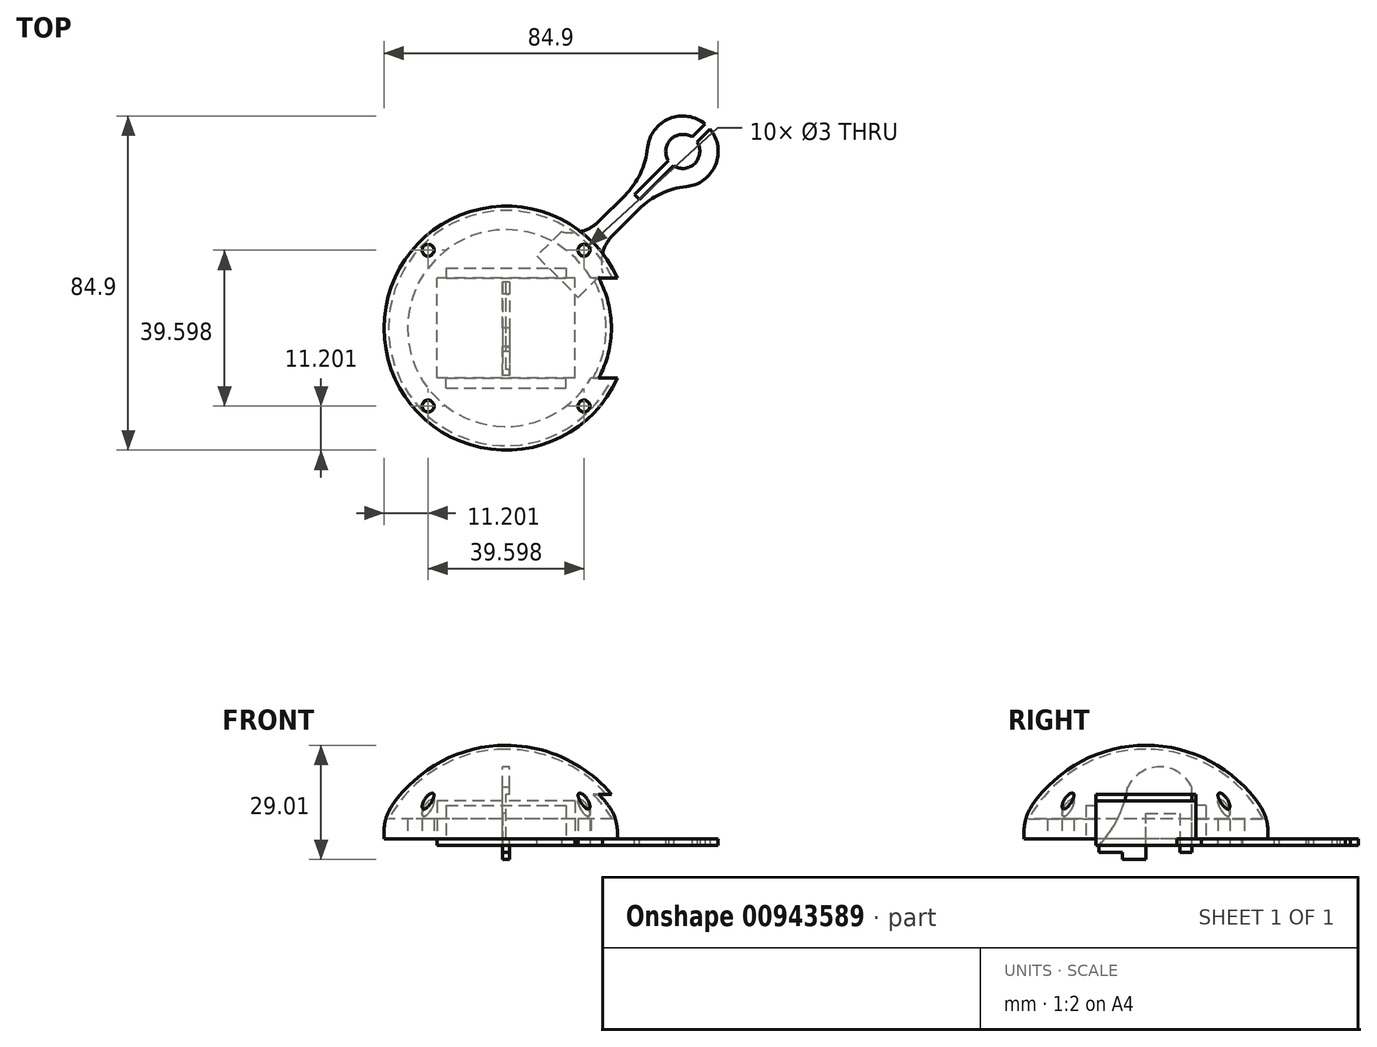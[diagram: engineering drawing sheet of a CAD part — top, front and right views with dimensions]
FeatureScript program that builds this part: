
annotation { "Feature Type Name" : "Feature", "Feature Type Description" : "" }
export const myFeature = defineFeature(function(context is Context, id is Id, definition is map)
    precondition{}
    {
        {
            var Q0;
            Q0=qCreatedBy(makeId("Top.planeOp"),FACE);
            var sketch = newSketch(context, id + "F0", { "sketchPlane" : qUnion([Q0])});
            skCircle(sketch, "E0", {"center": v(0, 0) * mm, "radius": 25 * mm, "construction": true});
            skArc(sketch, "E1", {"start": v(-25.2, 12.18) * mm, "mid": v(-26.92, 7.7) * mm, "end": v(-27.84, 3) * mm});
            skLineSegment(sketch, "E2", {"start": v(-44.9, -44.9) * mm, "end": v(44.9, 44.9) * mm, "construction": true});
            skLineSegment(sketch, "E3", {"start": v(-44.9, 44.9) * mm, "end": v(44.9, -44.9) * mm, "construction": true});
            skCircle(sketch, "E4", {"center": v(0, 28) * mm, "radius": 1.5 * mm});
            skCircle(sketch, "E5", {"center": v(-19.8, 19.8) * mm, "radius": 1.5 * mm});
            skCircle(sketch, "E6", {"center": v(-28, 0) * mm, "radius": 1.5 * mm});
            skCircle(sketch, "E7", {"center": v(-19.8, -19.8) * mm, "radius": 1.5 * mm});
            skCircle(sketch, "E8", {"center": v(0, -28) * mm, "radius": 1.5 * mm});
            skCircle(sketch, "E9", {"center": v(19.8, -19.8) * mm, "radius": 1.5 * mm});
            skCircle(sketch, "E10", {"center": v(28, 0) * mm, "radius": 1.5 * mm});
            skCircle(sketch, "E11", {"center": v(19.8, 19.8) * mm, "radius": 1.5 * mm});
            skArc(sketch, "E12", {"start": v(3, 27.84) * mm, "mid": v(0, 31) * mm, "end": v(-3, 27.84) * mm});
            skArc(sketch, "E13", {"start": v(27.84, -3) * mm, "mid": v(31, 0) * mm, "end": v(27.84, 3) * mm});
            skArc(sketch, "E14", {"start": v(-3, -27.84) * mm, "mid": v(0, -31) * mm, "end": v(3, -27.84) * mm});
            skArc(sketch, "E15", {"start": v(-27.84, 3) * mm, "mid": v(-31, 0) * mm, "end": v(-27.84, -3) * mm});
            skArc(sketch, "E16.trimOffspring", {"start": v(12.18, 25.2) * mm, "mid": v(7.7, 26.92) * mm, "end": v(3, 27.84) * mm});
            skArc(sketch, "E17.trimOffspring", {"start": v(3, -27.84) * mm, "mid": v(7.7, -26.92) * mm, "end": v(12.18, -25.2) * mm});
            skArc(sketch, "E18.trimOffspring", {"start": v(-12.18, -25.2) * mm, "mid": v(-7.7, -26.92) * mm, "end": v(-3, -27.84) * mm});
            skArc(sketch, "E19", {"start": v(45.82, 35.95) * mm, "mid": v(51.27, 51.27) * mm, "end": v(35.95, 45.82) * mm});
            skArc(sketch, "E20", {"start": v(35.95, -45.82) * mm, "mid": v(51.27, -51.27) * mm, "end": v(45.82, -35.95) * mm});
            skArc(sketch, "E21", {"start": v(-45.82, -35.95) * mm, "mid": v(-51.27, -51.27) * mm, "end": v(-35.95, -45.82) * mm});
            skArc(sketch, "E22", {"start": v(-35.95, 45.82) * mm, "mid": v(-51.27, 51.27) * mm, "end": v(-45.82, 35.95) * mm});
            skLineSegment(sketch, "E23", {"start": v(23.6, 27.14) * mm, "end": v(30.2, 33.73) * mm});
            skLineSegment(sketch, "E24", {"start": v(33.73, 30.2) * mm, "end": v(27.14, 23.6) * mm});
            skLineSegment(sketch, "E25", {"start": v(33.73, -30.2) * mm, "end": v(27.14, -23.6) * mm});
            skLineSegment(sketch, "E26", {"start": v(30.2, -33.73) * mm, "end": v(23.6, -27.14) * mm});
            skLineSegment(sketch, "E27", {"start": v(-30.2, -33.73) * mm, "end": v(-23.6, -27.14) * mm});
            skLineSegment(sketch, "E28", {"start": v(-33.73, -30.2) * mm, "end": v(-27.14, -23.6) * mm});
            skLineSegment(sketch, "E29", {"start": v(-33.73, 30.2) * mm, "end": v(-27.14, 23.6) * mm});
            skLineSegment(sketch, "E30", {"start": v(-30.2, 33.73) * mm, "end": v(-23.6, 27.14) * mm});
            skCircle(sketch, "E31", {"center": v(44.9, 44.9) * mm, "radius": 4.33 * mm});
            skCircle(sketch, "E32", {"center": v(44.9, -44.9) * mm, "radius": 4.33 * mm});
            skCircle(sketch, "E33", {"center": v(-44.9, -44.9) * mm, "radius": 4.33 * mm});
            skCircle(sketch, "E34", {"center": v(-44.9, 44.9) * mm, "radius": 4.33 * mm});
            skPoint(sketch, "E35.visualSharp", {"position": v(40.56, -37.02) * mm});
            skArc(sketch, "E35.filletArc", {"start": v(33.73, -30.2) * mm, "mid": v(39.28, -34.11) * mm, "end": v(45.82, -35.95) * mm});
            skPoint(sketch, "E36.visualSharp", {"position": v(37.02, -40.56) * mm});
            skArc(sketch, "E36.filletArc", {"start": v(35.95, -45.82) * mm, "mid": v(34.11, -39.28) * mm, "end": v(30.2, -33.73) * mm});
            skPoint(sketch, "E37.visualSharp", {"position": v(-37.02, -40.56) * mm});
            skArc(sketch, "E37.filletArc", {"start": v(-30.2, -33.73) * mm, "mid": v(-34.11, -39.28) * mm, "end": v(-35.95, -45.82) * mm});
            skPoint(sketch, "E38.visualSharp", {"position": v(-40.56, -37.02) * mm});
            skArc(sketch, "E38.filletArc", {"start": v(-45.82, -35.95) * mm, "mid": v(-39.28, -34.11) * mm, "end": v(-33.73, -30.2) * mm});
            skPoint(sketch, "E39.visualSharp", {"position": v(-40.56, 37.02) * mm});
            skArc(sketch, "E39.filletArc", {"start": v(-33.73, 30.2) * mm, "mid": v(-39.28, 34.11) * mm, "end": v(-45.82, 35.95) * mm});
            skPoint(sketch, "E40.visualSharp", {"position": v(-37.02, 40.56) * mm});
            skArc(sketch, "E40.filletArc", {"start": v(-35.95, 45.82) * mm, "mid": v(-34.11, 39.28) * mm, "end": v(-30.2, 33.73) * mm});
            skPoint(sketch, "E41.visualSharp", {"position": v(37.02, 40.56) * mm});
            skArc(sketch, "E41.filletArc", {"start": v(30.2, 33.73) * mm, "mid": v(34.11, 39.28) * mm, "end": v(35.95, 45.82) * mm});
            skPoint(sketch, "E42.visualSharp", {"position": v(40.56, 37.02) * mm});
            skArc(sketch, "E42.filletArc", {"start": v(45.82, 35.95) * mm, "mid": v(39.28, 34.11) * mm, "end": v(33.73, 30.2) * mm});
            skArc(sketch, "E43.filletArc", {"start": v(23.6, -27.14) * mm, "mid": v(18.2, -24.35) * mm, "end": v(12.18, -25.2) * mm});
            skArc(sketch, "E44", {"start": v(-12.18, -25.2) * mm, "mid": v(0, -28) * mm, "end": v(12.18, -25.2) * mm});
            skArc(sketch, "E45.filletArc", {"start": v(-12.18, -25.2) * mm, "mid": v(-18.2, -24.35) * mm, "end": v(-23.6, -27.14) * mm});
            skArc(sketch, "E46.filletArc", {"start": v(-25.2, 12.18) * mm, "mid": v(-24.35, 18.2) * mm, "end": v(-27.14, 23.6) * mm});
            skArc(sketch, "E47.filletArc", {"start": v(12.18, 25.2) * mm, "mid": v(18.2, 24.35) * mm, "end": v(23.6, 27.14) * mm});
            skPoint(sketch, "E48.visualSharp", {"position": v(-21.49, -17.95) * mm});
            skArc(sketch, "E48.filletArc", {"start": v(-27.14, -23.6) * mm, "mid": v(-24.35, -18.2) * mm, "end": v(-25.2, -12.18) * mm});
            skArc(sketch, "E49.trimOffspring", {"start": v(25.2, -12.18) * mm, "mid": v(26.92, -7.7) * mm, "end": v(27.84, -3) * mm});
            skPoint(sketch, "E50.visualSharp", {"position": v(21.49, -17.95) * mm});
            skArc(sketch, "E50.filletArc", {"start": v(25.2, -12.18) * mm, "mid": v(24.35, -18.2) * mm, "end": v(27.14, -23.6) * mm});
            skArc(sketch, "E51.trimOffspring", {"start": v(27.84, 3) * mm, "mid": v(26.92, 7.7) * mm, "end": v(25.2, 12.18) * mm});
            skPoint(sketch, "E52.visualSharp", {"position": v(21.49, 17.95) * mm});
            skArc(sketch, "E52.filletArc", {"start": v(27.14, 23.6) * mm, "mid": v(24.35, 18.2) * mm, "end": v(25.2, 12.18) * mm});
            skArc(sketch, "E53.trimOffspring", {"start": v(-3, 27.84) * mm, "mid": v(-7.7, 26.92) * mm, "end": v(-12.18, 25.2) * mm});
            skPoint(sketch, "E54.visualSharp", {"position": v(-17.95, 21.49) * mm});
            skArc(sketch, "E54.filletArc", {"start": v(-23.6, 27.14) * mm, "mid": v(-18.2, 24.35) * mm, "end": v(-12.18, 25.2) * mm});
            skArc(sketch, "E55.trimOffspring", {"start": v(-27.84, -3) * mm, "mid": v(-26.92, -7.7) * mm, "end": v(-25.2, -12.18) * mm});
            skSolve(sketch);
        }
        {
            var Q0;
            Q0 = qSketchRegion(id + "F0", true);
            extrude(context, id + "F1", {"entities" : qUnion([Q0]), "depth" : 1.7 * mm, "offsetDistance" : 25 * mm});
        }
        {
            var Q0;
            Q0=qCreatedBy(makeId("Top.planeOp"),FACE);
            var sketch = newSketch(context, id + "F2", { "sketchPlane" : qUnion([Q0])});
            skLineSegment(sketch, "E56", {"start": v(0, 0) * mm, "end": v(-50.91, -50.91) * mm, "construction": true});
            skLineSegment(sketch, "E57", {"start": v(-44.03, -45.3) * mm, "end": v(-36.96, -38.23) * mm});
            skLineSegment(sketch, "E58", {"start": v(-36.96, -38.23) * mm, "end": v(-38.23, -36.96) * mm});
            skLineSegment(sketch, "E59", {"start": v(-38.23, -36.96) * mm, "end": v(-45.3, -44.03) * mm});
            skLineSegment(sketch, "E60", {"start": v(-45.3, -44.03) * mm, "end": v(-44.03, -45.3) * mm});
            skLineSegment(sketch, "E61.MirrorCS", {"start": v(-36.96, 38.23) * mm, "end": v(-38.23, 36.96) * mm});
            skLineSegment(sketch, "E62.MirrorCS", {"start": v(-45.3, 44.03) * mm, "end": v(-44.03, 45.3) * mm});
            skLineSegment(sketch, "E63.MirrorCS", {"start": v(-44.03, 45.3) * mm, "end": v(-36.96, 38.23) * mm});
            skLineSegment(sketch, "E64.MirrorCS", {"start": v(-38.23, 36.96) * mm, "end": v(-45.3, 44.03) * mm});
            skLineSegment(sketch, "E65.MirrorCS", {"start": v(45.3, -44.03) * mm, "end": v(44.03, -45.3) * mm});
            skLineSegment(sketch, "E66.MirrorCS", {"start": v(36.96, 38.23) * mm, "end": v(38.23, 36.96) * mm});
            skLineSegment(sketch, "E67.MirrorCS", {"start": v(36.96, -38.23) * mm, "end": v(38.23, -36.96) * mm});
            skLineSegment(sketch, "E68.MirrorCS", {"start": v(45.3, 44.03) * mm, "end": v(44.03, 45.3) * mm});
            skLineSegment(sketch, "E69.MirrorCS", {"start": v(44.03, -45.3) * mm, "end": v(36.96, -38.23) * mm});
            skLineSegment(sketch, "E70.MirrorCS", {"start": v(44.03, 45.3) * mm, "end": v(36.96, 38.23) * mm});
            skLineSegment(sketch, "E71.MirrorCS", {"start": v(38.23, 36.96) * mm, "end": v(45.3, 44.03) * mm});
            skLineSegment(sketch, "E72.MirrorCS", {"start": v(38.23, -36.96) * mm, "end": v(45.3, -44.03) * mm});
            skSolve(sketch);
        }
        {
            var Q0;
            Q0 = qSketchRegion(id + "F2", true);
            extrude(context, id + "F3", {"entities" : qUnion([Q0]), "operationType" : NewBodyOperationType.REMOVE, "endBound" : BoundingType.SYMMETRIC, "oppositeDirection" : true, "depth" : 25 * mm, "offsetDistance" : 25 * mm});
        }
        {
            var Q0;
            Q0=makeQuery(id+"F1.opExtrude","SWEPT_BODY",BODY,{"disambiguationData":[OSD([sQuery(id+"F0.wireOp",EDGE,"E4"),sQuery(id+"F0.wireOp",EDGE,"E5"),sQuery(id+"F0.wireOp",EDGE,"E6"),sQuery(id+"F0.wireOp",EDGE,"E7"),sQuery(id+"F0.wireOp",EDGE,"E8"),sQuery(id+"F0.wireOp",EDGE,"E9"),sQuery(id+"F0.wireOp",EDGE,"E10"),sQuery(id+"F0.wireOp",EDGE,"E11"),sQuery(id+"F0.wireOp",EDGE,"E12"),sQuery(id+"F0.wireOp",EDGE,"E13"),sQuery(id+"F0.wireOp",EDGE,"E14"),sQuery(id+"F0.wireOp",EDGE,"E15"),sQuery(id+"F0.wireOp",EDGE,"E19"),sQuery(id+"F0.wireOp",EDGE,"E20"),sQuery(id+"F0.wireOp",EDGE,"E21"),sQuery(id+"F0.wireOp",EDGE,"E22"),sQuery(id+"F0.wireOp",EDGE,"E23"),sQuery(id+"F0.wireOp",EDGE,"E24"),sQuery(id+"F0.wireOp",EDGE,"E25"),sQuery(id+"F0.wireOp",EDGE,"E26"),sQuery(id+"F0.wireOp",EDGE,"E27"),sQuery(id+"F0.wireOp",EDGE,"E28"),sQuery(id+"F0.wireOp",EDGE,"E29"),sQuery(id+"F0.wireOp",EDGE,"E30"),sQuery(id+"F0.wireOp",EDGE,"E31"),sQuery(id+"F0.wireOp",EDGE,"E32"),sQuery(id+"F0.wireOp",EDGE,"E33"),sQuery(id+"F0.wireOp",EDGE,"E34"),sQuery(id+"F0.wireOp",EDGE,"E35.filletArc"),sQuery(id+"F0.wireOp",EDGE,"E36.filletArc"),sQuery(id+"F0.wireOp",EDGE,"E37.filletArc"),sQuery(id+"F0.wireOp",EDGE,"E38.filletArc"),sQuery(id+"F0.wireOp",EDGE,"E39.filletArc"),sQuery(id+"F0.wireOp",EDGE,"E40.filletArc"),sQuery(id+"F0.wireOp",EDGE,"E41.filletArc"),sQuery(id+"F0.wireOp",EDGE,"E42.filletArc"),sQuery(id+"F0.wireOp",EDGE,"E43.filletArc"),sQuery(id+"F0.wireOp",EDGE,"E44"),sQuery(id+"F0.wireOp",EDGE,"E45.filletArc"),sQuery(id+"F0.wireOp",EDGE,"E46.filletArc"),sQuery(id+"F0.wireOp",EDGE,"E47.filletArc"),sQuery(id+"F0.wireOp",EDGE,"E48.filletArc"),sQuery(id+"F0.wireOp",EDGE,"E49.trimOffspring"),sQuery(id+"F0.wireOp",EDGE,"E50.filletArc"),sQuery(id+"F0.wireOp",EDGE,"E51.trimOffspring"),sQuery(id+"F0.wireOp",EDGE,"E16.trimOffspring"),sQuery(id+"F0.wireOp",EDGE,"E52.filletArc"),sQuery(id+"F0.wireOp",EDGE,"E53.trimOffspring"),sQuery(id+"F0.wireOp",EDGE,"E1"),sQuery(id+"F0.wireOp",EDGE,"E54.filletArc"),sQuery(id+"F0.wireOp",EDGE,"E55.trimOffspring")])]});
            transform(context, id + "F4", {"entities" : qUnion([Q0]), "transformType" : TransformType.TRANSLATION_3D, "dx" : 0 * mm, "dy" : 0 * mm, "dz" : 0 * mm, "makeCopy" : true});
        }
        {
            var Q0;
            Q0=qCreatedBy(makeId("Top.planeOp"),FACE);
            var sketch = newSketch(context, id + "F5", { "sketchPlane" : qUnion([Q0])});
            skLineSegment(sketch, "E73", {"start": v(29.05, 39.54) * mm, "end": v(7.83, 18.33) * mm});
            skLineSegment(sketch, "E74", {"start": v(7.83, 18.33) * mm, "end": v(18.33, 7.83) * mm});
            skLineSegment(sketch, "E75", {"start": v(18.33, 7.83) * mm, "end": v(39.54, 29.05) * mm});
            skLineSegment(sketch, "E76", {"start": v(39.54, 29.05) * mm, "end": v(105, -36.42) * mm});
            skLineSegment(sketch, "E77", {"start": v(105, -36.42) * mm, "end": v(-36.42, -177.84) * mm});
            skLineSegment(sketch, "E78", {"start": v(-36.42, -177.84) * mm, "end": v(-177.84, -36.42) * mm});
            skLineSegment(sketch, "E79", {"start": v(-177.84, -36.42) * mm, "end": v(-36.42, 105) * mm});
            skLineSegment(sketch, "E80", {"start": v(-36.42, 105) * mm, "end": v(29.05, 39.54) * mm});
            skLineSegment(sketch, "E81", {"start": v(0, 0) * mm, "end": v(19.8, 19.8) * mm, "construction": true});
            skPoint(sketch, "E82", {"position": v(44.9, 44.9) * mm});
            skSolve(sketch);
        }
        {
            var Q0;
            Q0 = qSketchRegion(id + "F5", true);
            extrude(context, id + "F6", {"entities" : qUnion([Q0]), "operationType" : NewBodyOperationType.REMOVE, "endBound" : BoundingType.SYMMETRIC, "oppositeDirection" : true, "depth" : 25 * mm, "offsetDistance" : 25 * mm});
        }
        {
            var Q0;
            Q0=qCreatedBy(makeId("Top.planeOp"),FACE);
            var sketch = newSketch(context, id + "F7", { "sketchPlane" : qUnion([Q0])});
            skLineSegment(sketch, "E83", {"start": v(38.23, 36.96) * mm, "end": v(36.96, 38.23) * mm});
            skLineSegment(sketch, "E84", {"start": v(36.96, 38.23) * mm, "end": v(32.68, 33.95) * mm});
            skLineSegment(sketch, "E85", {"start": v(32.68, 33.95) * mm, "end": v(33.95, 32.68) * mm});
            skLineSegment(sketch, "E86", {"start": v(33.95, 32.68) * mm, "end": v(38.23, 36.96) * mm});
            skLineSegment(sketch, "E87", {"start": v(42.54, 41.27) * mm, "end": v(41.27, 42.54) * mm});
            skLineSegment(sketch, "E88", {"start": v(41.27, 42.54) * mm, "end": v(55.41, 56.68) * mm});
            skLineSegment(sketch, "E89", {"start": v(55.41, 56.68) * mm, "end": v(56.68, 55.41) * mm});
            skLineSegment(sketch, "E90", {"start": v(56.68, 55.41) * mm, "end": v(42.54, 41.27) * mm});
            skSolve(sketch);
        }
        {
            var Q0;
            Q0 = qSketchRegion(id + "F7", true);
            extrude(context, id + "F8", {"entities" : qUnion([Q0]), "operationType" : NewBodyOperationType.REMOVE, "endBound" : BoundingType.SYMMETRIC, "oppositeDirection" : true, "depth" : 25 * mm, "offsetDistance" : 25 * mm});
        }
        {
            var Q0;
            Q0=makeQuery(id+"F1.opExtrude","CAP_FACE",FACE,{"disambiguationData":[OSD([sQuery(id+"F0.wireOp",EDGE,"E4"),sQuery(id+"F0.wireOp",EDGE,"E5"),sQuery(id+"F0.wireOp",EDGE,"E6"),sQuery(id+"F0.wireOp",EDGE,"E7"),sQuery(id+"F0.wireOp",EDGE,"E8"),sQuery(id+"F0.wireOp",EDGE,"E9"),sQuery(id+"F0.wireOp",EDGE,"E10"),sQuery(id+"F0.wireOp",EDGE,"E11"),sQuery(id+"F0.wireOp",EDGE,"E12"),sQuery(id+"F0.wireOp",EDGE,"E13"),sQuery(id+"F0.wireOp",EDGE,"E14"),sQuery(id+"F0.wireOp",EDGE,"E15"),sQuery(id+"F0.wireOp",EDGE,"E19"),sQuery(id+"F0.wireOp",EDGE,"E20"),sQuery(id+"F0.wireOp",EDGE,"E21"),sQuery(id+"F0.wireOp",EDGE,"E22"),sQuery(id+"F0.wireOp",EDGE,"E23"),sQuery(id+"F0.wireOp",EDGE,"E24"),sQuery(id+"F0.wireOp",EDGE,"E25"),sQuery(id+"F0.wireOp",EDGE,"E26"),sQuery(id+"F0.wireOp",EDGE,"E27"),sQuery(id+"F0.wireOp",EDGE,"E28"),sQuery(id+"F0.wireOp",EDGE,"E29"),sQuery(id+"F0.wireOp",EDGE,"E30"),sQuery(id+"F0.wireOp",EDGE,"E31"),sQuery(id+"F0.wireOp",EDGE,"E32"),sQuery(id+"F0.wireOp",EDGE,"E33"),sQuery(id+"F0.wireOp",EDGE,"E34"),sQuery(id+"F0.wireOp",EDGE,"E35.filletArc"),sQuery(id+"F0.wireOp",EDGE,"E36.filletArc"),sQuery(id+"F0.wireOp",EDGE,"E37.filletArc"),sQuery(id+"F0.wireOp",EDGE,"E38.filletArc"),sQuery(id+"F0.wireOp",EDGE,"E39.filletArc"),sQuery(id+"F0.wireOp",EDGE,"E40.filletArc"),sQuery(id+"F0.wireOp",EDGE,"E41.filletArc"),sQuery(id+"F0.wireOp",EDGE,"E42.filletArc"),sQuery(id+"F0.wireOp",EDGE,"E43.filletArc"),sQuery(id+"F0.wireOp",EDGE,"E44"),sQuery(id+"F0.wireOp",EDGE,"E45.filletArc"),sQuery(id+"F0.wireOp",EDGE,"E46.filletArc"),sQuery(id+"F0.wireOp",EDGE,"E47.filletArc"),sQuery(id+"F0.wireOp",EDGE,"E48.filletArc"),sQuery(id+"F0.wireOp",EDGE,"E49.trimOffspring"),sQuery(id+"F0.wireOp",EDGE,"E50.filletArc"),sQuery(id+"F0.wireOp",EDGE,"E51.trimOffspring"),sQuery(id+"F0.wireOp",EDGE,"E16.trimOffspring"),sQuery(id+"F0.wireOp",EDGE,"E52.filletArc"),sQuery(id+"F0.wireOp",EDGE,"E53.trimOffspring"),sQuery(id+"F0.wireOp",EDGE,"E1"),sQuery(id+"F0.wireOp",EDGE,"E54.filletArc"),sQuery(id+"F0.wireOp",EDGE,"E55.trimOffspring")])],"isStart":false});
            var sketch = newSketch(context, id + "F9", { "sketchPlane" : qUnion([Q0])});
            skLineSegment(sketch, "E91.bottom", {"start": v(-15.24, -15.24) * mm, "end": v(15.24, -15.24) * mm});
            skLineSegment(sketch, "E91.top", {"start": v(-15.24, -12.7) * mm, "end": v(15.24, -12.7) * mm});
            skLineSegment(sketch, "E91.left", {"start": v(-15.24, -15.24) * mm, "end": v(-15.24, -12.7) * mm});
            skLineSegment(sketch, "E91.right", {"start": v(15.24, -15.24) * mm, "end": v(15.24, -12.7) * mm});
            skLineSegment(sketch, "E92.MirrorCS", {"start": v(15.24, 15.24) * mm, "end": v(15.24, 12.7) * mm});
            skLineSegment(sketch, "E93.MirrorCS", {"start": v(-15.24, 15.24) * mm, "end": v(-15.24, 12.7) * mm});
            skLineSegment(sketch, "E94.MirrorCS", {"start": v(-15.24, 15.24) * mm, "end": v(15.24, 15.24) * mm});
            skLineSegment(sketch, "E95.MirrorCS", {"start": v(-15.24, 12.7) * mm, "end": v(15.24, 12.7) * mm});
            skSolve(sketch);
        }
        {
            var Q0;
            Q0 = qSketchRegion(id + "F9", true);
            extrude(context, id + "F10", {"entities" : qUnion([Q0]), "depth" : 8.5 * mm, "offsetDistance" : 25 * mm});
        }
        {
            var Q0;
            Q0=qCreatedBy(makeId("Right.planeOp"),FACE);
            var sketch = newSketch(context, id + "F11", { "sketchPlane" : qUnion([Q0])});
            skLineSegment(sketch, "E96", {"start": v(0, -3.56) * mm, "end": v(-6, -3.56) * mm});
            skLineSegment(sketch, "E97", {"start": v(-6, -3.56) * mm, "end": v(-6, -1.78) * mm});
            skLineSegment(sketch, "E98", {"start": v(-6, -1.78) * mm, "end": v(-11.98, -1.78) * mm});
            skLineSegment(sketch, "E99", {"start": v(-11.98, -1.78) * mm, "end": v(-11.98, 0) * mm});
            skLineSegment(sketch, "E100", {"start": v(0, -3.56) * mm, "end": v(0, 8.16) * mm});
            skLineSegment(sketch, "E101", {"start": v(0, 8.16) * mm, "end": v(8.66, 8.16) * mm});
            skLineSegment(sketch, "E102", {"start": v(8.66, 8.16) * mm, "end": v(8.66, -1.78) * mm});
            skLineSegment(sketch, "E103", {"start": v(8.66, -1.78) * mm, "end": v(11.66, -1.78) * mm});
            skLineSegment(sketch, "E104", {"start": v(11.66, -1.78) * mm, "end": v(11.66, 14.72) * mm});
            skArc(sketch, "E105", {"start": v(11.66, 14.72) * mm, "mid": v(3.5, 19.97) * mm, "end": v(-4.66, 14.72) * mm});
            skArc(sketch, "E106", {"start": v(-11.98, 0) * mm, "mid": v(-7.18, 6.8) * mm, "end": v(-4.66, 14.72) * mm});
            skSolve(sketch);
        }
        {
            var Q0;
            Q0 = qSketchRegion(id + "F11", true);
            extrude(context, id + "F12", {"entities" : qUnion([Q0]), "endBound" : BoundingType.SYMMETRIC, "depth" : 1.78 * mm, "offsetDistance" : 25 * mm});
        }
        {
            var Q0;
            Q0=makeQuery(id+"F1.opExtrude","CAP_FACE",FACE,{"disambiguationData":[OSD([sQuery(id+"F0.wireOp",EDGE,"E4"),sQuery(id+"F0.wireOp",EDGE,"E5"),sQuery(id+"F0.wireOp",EDGE,"E6"),sQuery(id+"F0.wireOp",EDGE,"E7"),sQuery(id+"F0.wireOp",EDGE,"E8"),sQuery(id+"F0.wireOp",EDGE,"E9"),sQuery(id+"F0.wireOp",EDGE,"E10"),sQuery(id+"F0.wireOp",EDGE,"E11"),sQuery(id+"F0.wireOp",EDGE,"E12"),sQuery(id+"F0.wireOp",EDGE,"E13"),sQuery(id+"F0.wireOp",EDGE,"E14"),sQuery(id+"F0.wireOp",EDGE,"E15"),sQuery(id+"F0.wireOp",EDGE,"E19"),sQuery(id+"F0.wireOp",EDGE,"E20"),sQuery(id+"F0.wireOp",EDGE,"E21"),sQuery(id+"F0.wireOp",EDGE,"E22"),sQuery(id+"F0.wireOp",EDGE,"E23"),sQuery(id+"F0.wireOp",EDGE,"E24"),sQuery(id+"F0.wireOp",EDGE,"E25"),sQuery(id+"F0.wireOp",EDGE,"E26"),sQuery(id+"F0.wireOp",EDGE,"E27"),sQuery(id+"F0.wireOp",EDGE,"E28"),sQuery(id+"F0.wireOp",EDGE,"E29"),sQuery(id+"F0.wireOp",EDGE,"E30"),sQuery(id+"F0.wireOp",EDGE,"E31"),sQuery(id+"F0.wireOp",EDGE,"E32"),sQuery(id+"F0.wireOp",EDGE,"E33"),sQuery(id+"F0.wireOp",EDGE,"E34"),sQuery(id+"F0.wireOp",EDGE,"E35.filletArc"),sQuery(id+"F0.wireOp",EDGE,"E36.filletArc"),sQuery(id+"F0.wireOp",EDGE,"E37.filletArc"),sQuery(id+"F0.wireOp",EDGE,"E38.filletArc"),sQuery(id+"F0.wireOp",EDGE,"E39.filletArc"),sQuery(id+"F0.wireOp",EDGE,"E40.filletArc"),sQuery(id+"F0.wireOp",EDGE,"E41.filletArc"),sQuery(id+"F0.wireOp",EDGE,"E42.filletArc"),sQuery(id+"F0.wireOp",EDGE,"E43.filletArc"),sQuery(id+"F0.wireOp",EDGE,"E44"),sQuery(id+"F0.wireOp",EDGE,"E45.filletArc"),sQuery(id+"F0.wireOp",EDGE,"E46.filletArc"),sQuery(id+"F0.wireOp",EDGE,"E47.filletArc"),sQuery(id+"F0.wireOp",EDGE,"E48.filletArc"),sQuery(id+"F0.wireOp",EDGE,"E49.trimOffspring"),sQuery(id+"F0.wireOp",EDGE,"E50.filletArc"),sQuery(id+"F0.wireOp",EDGE,"E51.trimOffspring"),sQuery(id+"F0.wireOp",EDGE,"E16.trimOffspring"),sQuery(id+"F0.wireOp",EDGE,"E52.filletArc"),sQuery(id+"F0.wireOp",EDGE,"E53.trimOffspring"),sQuery(id+"F0.wireOp",EDGE,"E1"),sQuery(id+"F0.wireOp",EDGE,"E54.filletArc"),sQuery(id+"F0.wireOp",EDGE,"E55.trimOffspring")])],"isStart":false});
            var sketch = newSketch(context, id + "F13", { "sketchPlane" : qUnion([Q0])});
            skCircle(sketch, "E107", {"center": v(0, 0) * mm, "radius": 31 * mm});
            skCircle(sketch, "E108", {"center": v(0, 0) * mm, "radius": 25 * mm});
            skCircle(sketch, "E109", {"center": v(-19.8, 19.8) * mm, "radius": 1.5 * mm});
            skCircle(sketch, "E110", {"center": v(-19.8, -19.8) * mm, "radius": 1.5 * mm});
            skCircle(sketch, "E111.MirrorC", {"center": v(19.8, -19.8) * mm, "radius": 1.5 * mm});
            skCircle(sketch, "E112.MirrorC", {"center": v(19.8, 19.8) * mm, "radius": 1.5 * mm});
            skSolve(sketch);
        }
        {
            var Q0;
            Q0 = qSketchRegion(id + "F13", true);
            extrude(context, id + "F14", {"entities" : qUnion([Q0]), "depth" : 5 * mm, "offsetDistance" : 25 * mm});
        }
        {
            var Q0;
            Q0=qCreatedBy(makeId("Front.planeOp"),FACE);
            var sketch = newSketch(context, id + "F15", { "sketchPlane" : qUnion([Q0])});
            skArc(sketch, "E113", {"start": v(31, 6.7) * mm, "mid": v(18.12, 20.4) * mm, "end": v(0, 25.45) * mm});
            skLineSegment(sketch, "E114", {"start": v(0, 6.7) * mm, "end": v(31, 6.7) * mm});
            skLineSegment(sketch, "E115", {"start": v(0, 25.45) * mm, "end": v(0, 6.7) * mm});
            skPoint(sketch, "E116.orphan", {"position": v(-31, 6.7) * mm});
            skArc(sketch, "E117", {"start": v(29.87, 6.7) * mm, "mid": v(17.37, 19.68) * mm, "end": v(0, 24.45) * mm});
            skSolve(sketch);
        }
        {
            var Q0;
            {var subQ0=sQuery(id+"F15.wireOp",EDGE,"E113");Q0=makeQuery(id+"F15.imprint","IMPRINT",FACE,{"disambiguationData":[TD([[makeQuery(id+"F15.imprint","IMPRINT",EDGE,{"derivedFrom":subQ0}),1.0]])]});}
            var Q1;
            Q1=sQuery(id+"F15.wireOp",EDGE,"E115");
            revolve(context, id + "F16", {"operationType" : NewBodyOperationType.ADD, "surfaceOperationType" : NewSurfaceOperationType.NEW, "entities" : qUnion([Q0]), "axis" : qUnion([Q1]), "revolveType" : RevolveType.FULL});
        }
        {
            var Q0;
            Q0=makeQuery(id+"F14.opExtrude","CAP_FACE",FACE,{"disambiguationData":[OSD([sQuery(id+"F13.wireOp",EDGE,"E107"),sQuery(id+"F13.wireOp",EDGE,"E108"),sQuery(id+"F13.wireOp",EDGE,"E109"),sQuery(id+"F13.wireOp",EDGE,"E110"),sQuery(id+"F13.wireOp",EDGE,"E111.MirrorC"),sQuery(id+"F13.wireOp",EDGE,"E112.MirrorC")])],"isStart":true});
            var sketch = newSketch(context, id + "F17", { "sketchPlane" : qUnion([Q0])});
            skCircle(sketch, "E118", {"center": v(19.8, 19.8) * mm, "radius": 1.5 * mm});
            skCircle(sketch, "E119.MirrorC", {"center": v(-19.8, 19.8) * mm, "radius": 1.5 * mm});
            skCircle(sketch, "E120.MirrorC", {"center": v(19.8, -19.8) * mm, "radius": 1.5 * mm});
            skCircle(sketch, "E121.MirrorC", {"center": v(-19.8, -19.8) * mm, "radius": 1.5 * mm});
            skSolve(sketch);
        }
        {
            var Q0;
            Q0 = qSketchRegion(id + "F17", true);
            extrude(context, id + "F18", {"entities" : qUnion([Q0]), "operationType" : NewBodyOperationType.REMOVE, "oppositeDirection" : true, "depth" : 25 * mm, "offsetDistance" : 25 * mm});
        }
        {
            var Q0;
            Q0=makeQuery(id+"F16.boolean.opBoolean","MERGE",EDGE,{"derivedFrom":[makeQuery(id+"F14.opExtrude","CAP_EDGE",EDGE,{"disambiguationData":[OSD([sQuery(id+"F13.wireOp",EDGE,"E107")])],"isStart":false}),makeQuery(id+"F16.opRevolve","SWEPT_EDGE",EDGE,{"disambiguationData":[OSD([sQuery(id+"F15.wireOp",EDGE,"E113"),sQuery(id+"F15.wireOp",EDGE,"E114")])]})]});
            fillet(context, id + "F19", {"entities" : qUnion([Q0]), "radius" : 12 * mm, "tangentPropagation" : true, "allowEdgeOverflow" : false});
        }
        {
            var Q0;
            Q0=qCreatedBy(makeId("Right.planeOp"),FACE);
            var sketch = newSketch(context, id + "F20", { "sketchPlane" : qUnion([Q0])});
            skLineSegment(sketch, "E122.bottom", {"start": v(-12.7, 13) * mm, "end": v(12.7, 13) * mm});
            skLineSegment(sketch, "E122.top", {"start": v(-12.7, 1.7) * mm, "end": v(12.7, 1.7) * mm});
            skLineSegment(sketch, "E122.left", {"start": v(-12.7, 13) * mm, "end": v(-12.7, 1.7) * mm});
            skLineSegment(sketch, "E122.right", {"start": v(12.7, 13) * mm, "end": v(12.7, 1.7) * mm});
            skSolve(sketch);
        }
        {
            var Q0;
            Q0 = qSketchRegion(id + "F20", true);
            extrude(context, id + "F21", {"entities" : qUnion([Q0]), "operationType" : NewBodyOperationType.REMOVE, "depth" : 300 * mm, "offsetDistance" : 25 * mm});
        }
        {
            var Q0;
            Q0=qCreatedBy(makeId("Top.planeOp"),FACE);
            var sketch = newSketch(context, id + "F22", { "sketchPlane" : qUnion([Q0])});
            skLineSegment(sketch, "E123.bottom", {"start": v(17.5, -12.7) * mm, "end": v(-17.5, -12.7) * mm});
            skLineSegment(sketch, "E123.top", {"start": v(17.5, 12.7) * mm, "end": v(-17.5, 12.7) * mm});
            skLineSegment(sketch, "E123.left", {"start": v(17.5, -12.7) * mm, "end": v(17.5, 12.7) * mm});
            skLineSegment(sketch, "E123.right", {"start": v(-17.5, -12.7) * mm, "end": v(-17.5, 12.7) * mm});
            skSolve(sketch);
        }
        {
            var Q0;
            Q0 = qSketchRegion(id + "F22", true);
            extrude(context, id + "F23", {"entities" : qUnion([Q0]), "depth" : 11.3 * mm, "offsetDistance" : 25 * mm});
        }
    });
